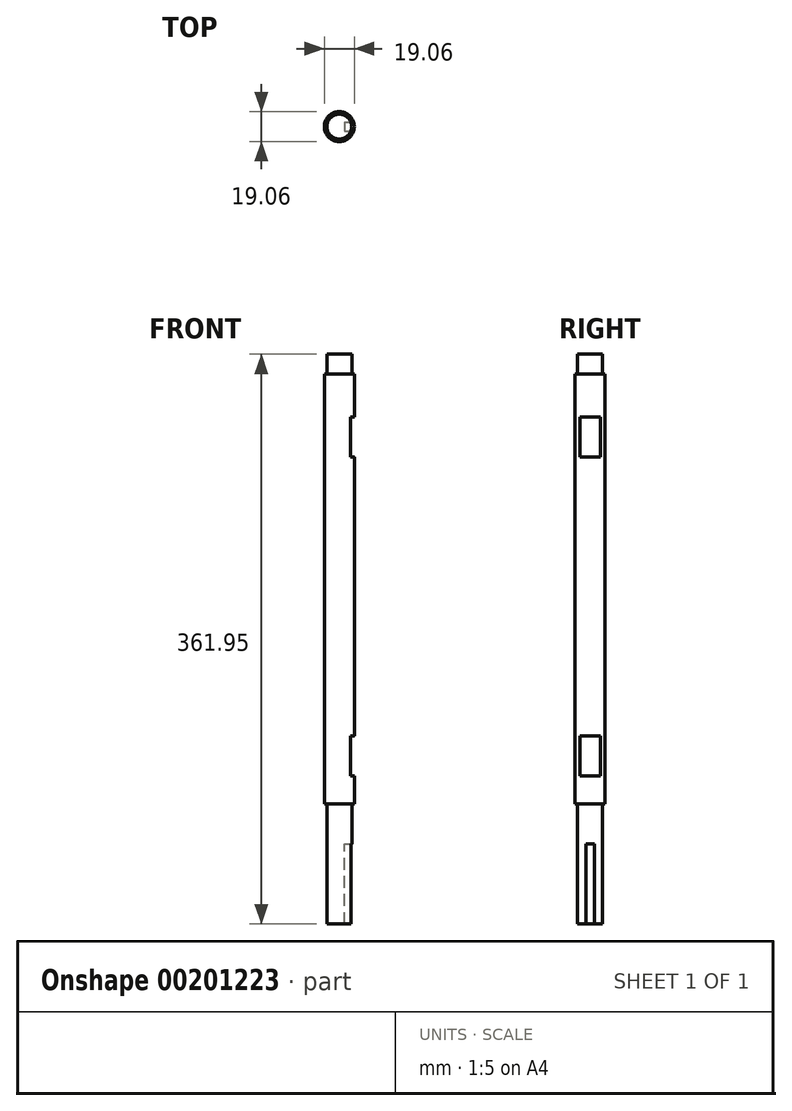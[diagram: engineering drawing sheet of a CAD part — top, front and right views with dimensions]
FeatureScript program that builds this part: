
annotation { "Feature Type Name" : "Feature", "Feature Type Description" : "" }
export const myFeature = defineFeature(function(context is Context, id is Id, definition is map)
    precondition{}
    {
        {
            var Q0;
            Q0=qCreatedBy(makeId("Top.planeOp"),FACE);
            var sketch = newSketch(context, id + "F0", { "sketchPlane" : qUnion([Q0])});
            skCircle(sketch, "E0", {"center": v(0, 0) * mm, "radius": 9.53 * mm});
            skCircle(sketch, "E1", {"center": v(0, 0) * mm, "radius": 7.94 * mm});
            skSolve(sketch);
        }
        {
            var Q0;
            Q0=makeQuery(id+"F0.imprint","IMPRINT",FACE,{"disambiguationData":[TD([[makeQuery(id+"F0.imprint","IMPRINT",EDGE,{"derivedFrom":sQuery(id+"F0.wireOp",EDGE,"E1")}),1.0]])]});
            extrude(context, id + "F1", {"entities" : qUnion([Q0]), "depth" : 361.95 * mm});
        }
        {
            var Q0;
            Q0 = qSketchRegion(id + "F0", true);
            extrude(context, id + "F2", {"entities" : qUnion([Q0]), "operationType" : NewBodyOperationType.ADD, "depth" : 349.25 * mm});
        }
        {
            var Q0;
            Q0 = qSketchRegion(id + "F0", true);
            extrude(context, id + "F3", {"entities" : qUnion([Q0]), "operationType" : NewBodyOperationType.REMOVE, "depth" : 76.2 * mm});
        }
        {
            var Q0;
            Q0=qCreatedBy(makeId("Right.planeOp"),FACE);
            cPlane(context, id + "F4", {"entities" : qUnion([Q0]), "cplaneType" : CPlaneType.OFFSET, "offset" : 7.94 * mm, "width" : 152.4 * mm, "height" : 152.4 * mm});
        }
        {
            var Q0;
            Q0=qCreatedBy(id+"F4.planeOp",FACE);
            var sketch = newSketch(context, id + "F5", { "sketchPlane" : qUnion([Q0])});
            skLineSegment(sketch, "E2.bottom", {"start": v(2.73, 0) * mm, "end": v(-2.73, 0) * mm});
            skLineSegment(sketch, "E2.top", {"start": v(2.73, 50.8) * mm, "end": v(-2.73, 50.8) * mm});
            skLineSegment(sketch, "E2.left", {"start": v(2.73, 0) * mm, "end": v(2.73, 50.8) * mm});
            skLineSegment(sketch, "E2.right", {"start": v(-2.73, 0) * mm, "end": v(-2.73, 50.8) * mm});
            skPoint(sketch, "E2.middle", {"position": v(0, 25.4) * mm});
            skSolve(sketch);
        }
        {
            var Q0;
            Q0=makeQuery(id+"F5.imprint","IMPRINT",FACE,{"disambiguationData":[TD([[makeQuery(id+"F5.imprint","IMPRINT",EDGE,{"derivedFrom":sQuery(id+"F5.wireOp",EDGE,"E2.bottom")}),-1.0]])]});
            extrude(context, id + "F6", {"entities" : qUnion([Q0]), "operationType" : NewBodyOperationType.REMOVE, "oppositeDirection" : true, "depth" : 4.76 * mm});
        }
        {
            var Q0;
            Q0=qCreatedBy(makeId("Right.planeOp"),FACE);
            cPlane(context, id + "F7", {"entities" : qUnion([Q0]), "cplaneType" : CPlaneType.OFFSET, "offset" : 9.52 * mm, "width" : 152.4 * mm, "height" : 152.4 * mm});
        }
        {
            var Q0;
            Q0=qCreatedBy(id+"F7.planeOp",FACE);
            var sketch = newSketch(context, id + "F8", { "sketchPlane" : qUnion([Q0])});
            skLineSegment(sketch, "E3.bottom", {"start": v(-12.7, 296.52) * mm, "end": v(12.7, 296.52) * mm});
            skLineSegment(sketch, "E3.top", {"start": v(-12.7, 321.92) * mm, "end": v(12.7, 321.92) * mm});
            skLineSegment(sketch, "E3.left", {"start": v(-12.7, 296.52) * mm, "end": v(-12.7, 321.92) * mm});
            skLineSegment(sketch, "E3.right", {"start": v(12.7, 296.52) * mm, "end": v(12.7, 321.92) * mm});
            skPoint(sketch, "E3.middle", {"position": v(0, 309.22) * mm});
            skLineSegment(sketch, "E4.bottom", {"start": v(12.7, 94.2) * mm, "end": v(-12.7, 94.2) * mm});
            skLineSegment(sketch, "E4.top", {"start": v(12.7, 119.6) * mm, "end": v(-12.7, 119.6) * mm});
            skLineSegment(sketch, "E4.left", {"start": v(12.7, 94.2) * mm, "end": v(12.7, 119.6) * mm});
            skLineSegment(sketch, "E4.right", {"start": v(-12.7, 94.2) * mm, "end": v(-12.7, 119.6) * mm});
            skPoint(sketch, "E4.middle", {"position": v(0, 106.9) * mm});
            skSolve(sketch);
        }
        {
            var Q0;
            Q0=makeQuery(id+"F8.imprint","IMPRINT",FACE,{"disambiguationData":[TD([[makeQuery(id+"F8.imprint","IMPRINT",EDGE,{"derivedFrom":sQuery(id+"F8.wireOp",EDGE,"E3.bottom")}),1.0]])]});
            var Q1;
            Q1=makeQuery(id+"F8.imprint","IMPRINT",FACE,{"disambiguationData":[TD([[makeQuery(id+"F8.imprint","IMPRINT",EDGE,{"derivedFrom":sQuery(id+"F8.wireOp",EDGE,"E4.bottom")}),-1.0]])]});
            extrude(context, id + "F9", {"entities" : qUnion([Q0, Q1]), "operationType" : NewBodyOperationType.REMOVE, "oppositeDirection" : true, "depth" : 2.54 * mm});
        }
    });
